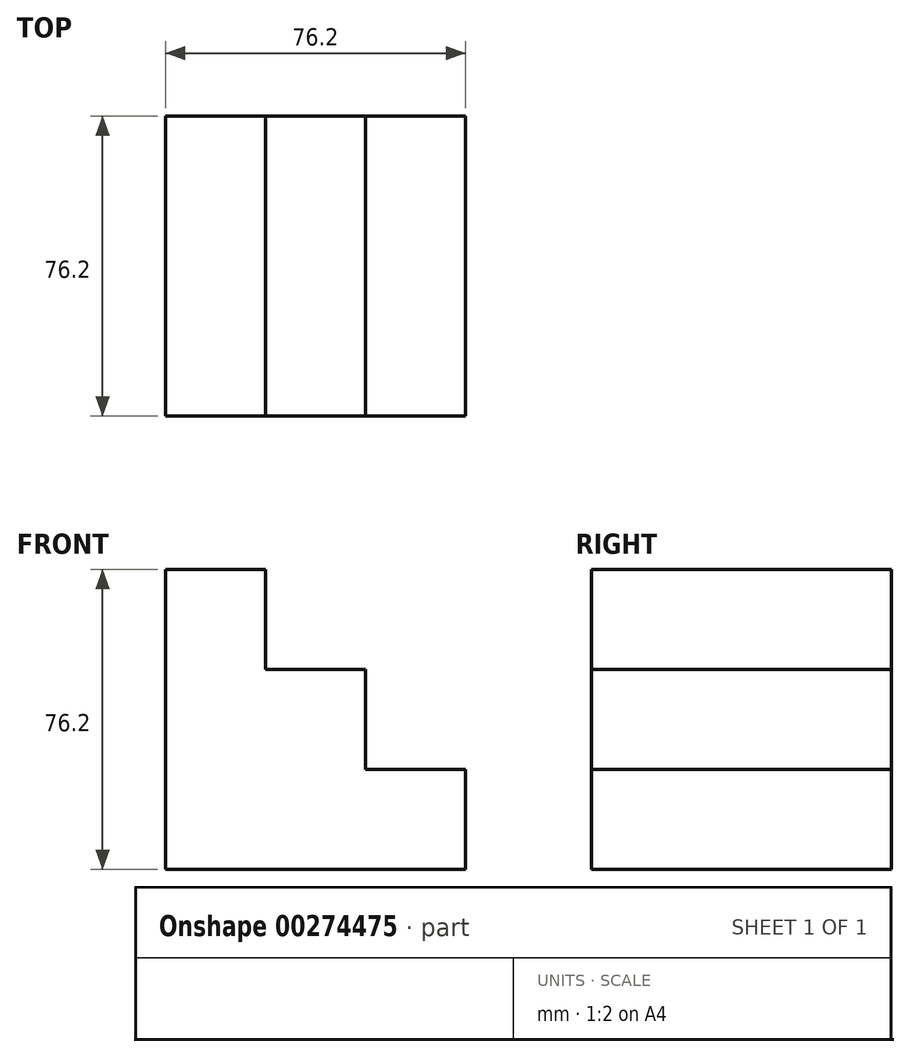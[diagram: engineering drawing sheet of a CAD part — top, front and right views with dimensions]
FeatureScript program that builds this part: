
annotation { "Feature Type Name" : "Feature", "Feature Type Description" : "" }
export const myFeature = defineFeature(function(context is Context, id is Id, definition is map)
    precondition{}
    {
        {
            var Q0;
            Q0=qCreatedBy(makeId("Front.planeOp"),FACE);
            var sketch = newSketch(context, id + "F0", { "sketchPlane" : qUnion([Q0])});
            skLineSegment(sketch, "E0", {"start": v(-56.59, 53.24) * mm, "end": v(-31.19, 53.24) * mm});
            skLineSegment(sketch, "E1", {"start": v(-31.19, 53.24) * mm, "end": v(-31.19, 27.84) * mm});
            skLineSegment(sketch, "E2", {"start": v(-31.19, 27.84) * mm, "end": v(-5.79, 27.84) * mm});
            skLineSegment(sketch, "E3", {"start": v(-5.79, 27.84) * mm, "end": v(-5.79, 2.44) * mm});
            skLineSegment(sketch, "E4", {"start": v(-5.79, 2.44) * mm, "end": v(19.61, 2.44) * mm});
            skLineSegment(sketch, "E5", {"start": v(19.61, 2.44) * mm, "end": v(19.61, -22.96) * mm});
            skLineSegment(sketch, "E6", {"start": v(19.61, -22.96) * mm, "end": v(-56.59, -22.96) * mm});
            skLineSegment(sketch, "E7", {"start": v(-56.59, -22.96) * mm, "end": v(-56.59, 53.24) * mm});
            skSolve(sketch);
        }
        {
            var Q0;
            Q0=makeQuery(id+"F0.imprint","IMPRINT",FACE,{"disambiguationData":[TD([[makeQuery(id+"F0.imprint","IMPRINT",EDGE,{"derivedFrom":sQuery(id+"F0.wireOp",EDGE,"E0")}),-1.0]])]});
            extrude(context, id + "F1", {"entities" : qUnion([Q0]), "depth" : 76.2 * mm});
        }
    });
